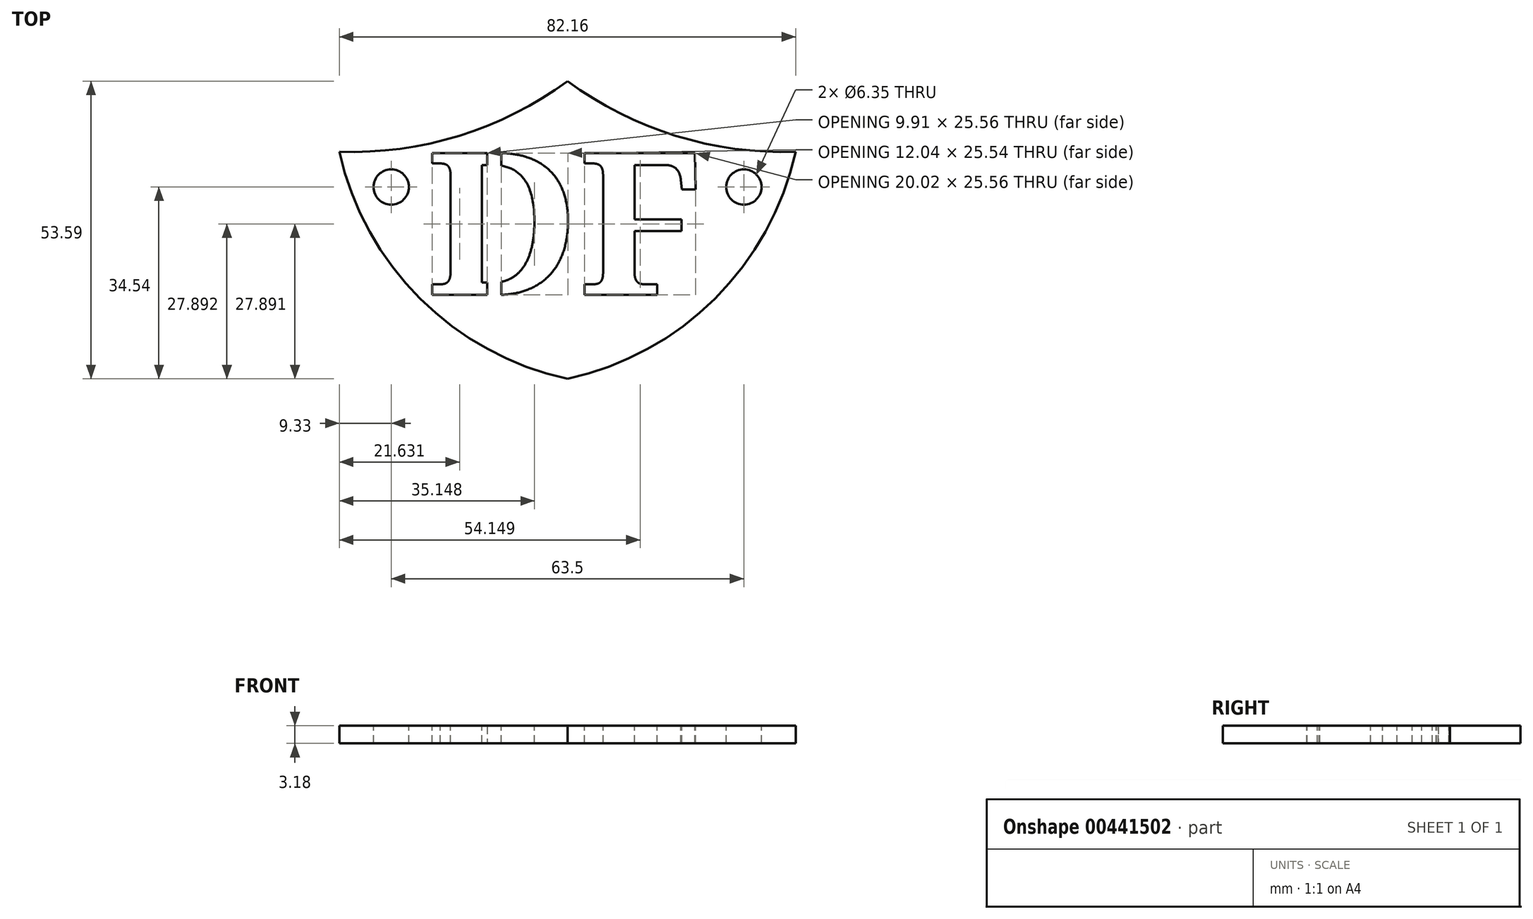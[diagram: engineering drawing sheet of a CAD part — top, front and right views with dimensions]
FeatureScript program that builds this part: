
annotation { "Feature Type Name" : "Feature", "Feature Type Description" : "" }
export const myFeature = defineFeature(function(context is Context, id is Id, definition is map)
    precondition{}
    {
        {
            var Q0;
            Q0=qCreatedBy(makeId("Top.planeOp"),FACE);
            var sketch = newSketch(context, id + "F0", { "sketchPlane" : qUnion([Q0])});
            skArc(sketch, "E0", {"start": v(-41.08, 0) * mm, "mid": v(-19.47, 2.88) * mm, "end": v(0, 12.7) * mm});
            skArc(sketch, "E1", {"start": v(-41.08, 0) * mm, "mid": v(-26.53, -26.46) * mm, "end": v(0, -40.9) * mm});
            skArc(sketch, "E2", {"start": v(0, -40.9) * mm, "mid": v(26.53, -26.46) * mm, "end": v(41.08, 0) * mm});
            skArc(sketch, "E3", {"start": v(0, 12.7) * mm, "mid": v(19.47, 2.88) * mm, "end": v(41.08, 0) * mm});
            skSolve(sketch);
        }
        {
            var Q0;
            Q0 = qSketchRegion(id + "F0", true);
            extrude(context, id + "F1", {"entities" : qUnion([Q0]), "depth" : 3.17 * mm});
        }
        {
            var Q0;
            Q0=makeQuery(id+"F1.opExtrude","CAP_FACE",FACE,{"disambiguationData":[OSD([sQuery(id+"F0.wireOp",EDGE,"E0"),sQuery(id+"F0.wireOp",EDGE,"E1"),sQuery(id+"F0.wireOp",EDGE,"E2"),sQuery(id+"F0.wireOp",EDGE,"E3")])],"isStart":false});
            var sketch = newSketch(context, id + "F2", { "sketchPlane" : qUnion([Q0])});
            skCircle(sketch, "E4", {"center": v(-31.75, -6.35) * mm, "radius": 3.18 * mm});
            skCircle(sketch, "E5", {"center": v(31.75, -6.35) * mm, "radius": 3.18 * mm});
            skText(sketch, "E6", { "text": "DF", "fontName": "NotoSerif-Bold.ttf"});
            const initialGuessF2  = {"E6": [-0.0254, -0.02578, 1, 0, 0.02578]};
            skSetInitialGuess(sketch, initialGuessF2);
            skSolve(sketch);
        }
        {
            var Q0;
            Q0 = qSketchRegion(id + "F2", true);
            extrude(context, id + "F3", {"entities" : qUnion([Q0]), "operationType" : NewBodyOperationType.REMOVE, "oppositeDirection" : true, "depth" : 25.4 * mm});
        }
        {
            var Q0;
            {var subQ0=sQuery(id+"F0.wireOp",EDGE,"E2");var subQ1=sQuery(id+"F0.wireOp",EDGE,"E0");var subQ2=sQuery(id+"F0.wireOp",EDGE,"E3");var subQ3=sQuery(id+"F0.wireOp",EDGE,"E1");Q0=makeQuery(id+"F3.boolean.opBoolean","SPLIT",FACE,{"disambiguationData":[TD([makeQuery(id+"F1.opExtrude","SWEPT_FACE",FACE,{"disambiguationData":[OSD([subQ1])]})])],"derivedFrom":makeQuery(id+"F1.opExtrude","CAP_FACE",FACE,{"disambiguationData":[OSD([subQ1,subQ3,subQ0,subQ2])],"isStart":false})});}
            var sketch = newSketch(context, id + "F4", { "sketchPlane" : qUnion([Q0])});
            skLineSegment(sketch, "E7.bottom", {"start": v(-14.5, 0.56) * mm, "end": v(-11.95, 0.56) * mm});
            skLineSegment(sketch, "E7.top", {"start": v(-14.5, -3.25) * mm, "end": v(-11.95, -3.25) * mm});
            skLineSegment(sketch, "E7.left", {"start": v(-14.5, 0.56) * mm, "end": v(-14.5, -3.25) * mm});
            skLineSegment(sketch, "E7.right", {"start": v(-11.95, 0.56) * mm, "end": v(-11.95, -3.25) * mm});
            skLineSegment(sketch, "E8.bottom", {"start": v(-14.5, -26.53) * mm, "end": v(-11.95, -26.53) * mm});
            skLineSegment(sketch, "E8.top", {"start": v(-14.5, -22.72) * mm, "end": v(-11.95, -22.72) * mm});
            skLineSegment(sketch, "E8.left", {"start": v(-14.5, -22.72) * mm, "end": v(-14.5, -26.53) * mm});
            skLineSegment(sketch, "E8.right", {"start": v(-11.95, -22.72) * mm, "end": v(-11.95, -26.53) * mm});
            skSolve(sketch);
        }
        {
            var Q0;
            Q0 = qSketchRegion(id + "F4", true);
            extrude(context, id + "F5", {"entities" : qUnion([Q0]), "operationType" : NewBodyOperationType.ADD, "oppositeDirection" : true, "depth" : 3.17 * mm});
        }
    });
